# Revit family: Shower-Handshower_Kit-KOHLER-ALEO-K-25107T_1
name_source: partatom
category: Plumbing Fixtures
units: mm (PartAtom-declared; Revit-internal decimal feet)

## family parameters
Cut with Voids When Loaded = No
Host = Face
OmniClass Number = 23.31.17.00
OmniClass Title = Showers
Part Type = Normal
Room Calculation Point = No
Round Connector Dimension = Use Diameter
Shared = No

## types (6) — shared parameters
ADA Compliant = No
Assembly Code = D2010700
CW Connection = Yes
Cold Water Inlet = Cold Water Inlet
Date Modified = 11/25/2022
Default Elevation = 42"
Drain Included = No
Flow Rate = 2 GPM
HW Connection = Yes
Handle Clearance = 3 3/8"
Height = 23 3/16"
Hot Water Inlet = Hot Water Inlet
Length = 7 1/2"
Manufacturer = Kohler Co.
Master Format 2014 = 22 42 23
Master Format 2014 Name = Residential Showers
Material = Premium Metal Construction
Pressure = 80.00 psi
Product Name = ALEO
Spout Reach = 7 1/2"
URL = http://www.kohler.com.cn
Vent Connection = No
Waste Connection = No
Waste Water Outlet = Waste Water Outlet
WaterSense Certified = No
Width = 8 1/4"

## per-type parameters (varying)
| type | 4 | 4F | Description | Finish | Model | Product Documentation Link | Product Page URL | Secondary Finish | Type |
| 4F, 2BL-Black | No | Yes | S Exposed Bath & Shower Faucet | KOHLER-Metal-2BL-Black | K-25107T-4F-2BL |  |  | Kohler-Plastic-58-Thunder_Grey | 1 |
| 4F, BL-Matte Black | No | Yes | S Exposed Bath & Shower Faucet | Kohler-Metal-BL-Matte_Black | K-25107T-4F-BL |  |  | Kohler-Plastic-58-Thunder_Grey | 2 |
| 4F, CP-Polished Chrome | No | Yes | S Exposed Bath & Shower Faucet | Kohler-Metal-CP-Polished_Chrome | K-25107T-4F-CP |  |  | Kohler-Plastic-0-White | 3 |
| 4, 2BL-Black | Yes | No | Wall-mounted Bathtub Shower Faucet (Smart Style) | KOHLER-Metal-2BL-Black | K-25107T-4-2BL | https://files.kohler.com.cn | https://www.kohler.com.cn | Kohler-Plastic-58-Thunder_Grey | 4 |
| 4, BL-Matte Black | Yes | No | Wall-mounted Bathtub Shower Faucet (Smart Style) | Kohler-Metal-BL-Matte_Black | K-25107T-4-BL | https://files.kohler.com.cn |  | Kohler-Plastic-58-Thunder_Grey | 5 |
| 4, CP- Polished Chrome | Yes | No | Wall-mounted Bathtub Shower Faucet (Smart Style) | Kohler-Metal-CP-Polished_Chrome | K-25107T-4-CP | https://files.kohler.com.cn | https://www.kohler.com.cn | Kohler-Plastic-0-White | 6 |

## geometry (parser evidence)
native form markers: Sweep x5
no freeform markers — native parametric forms only
